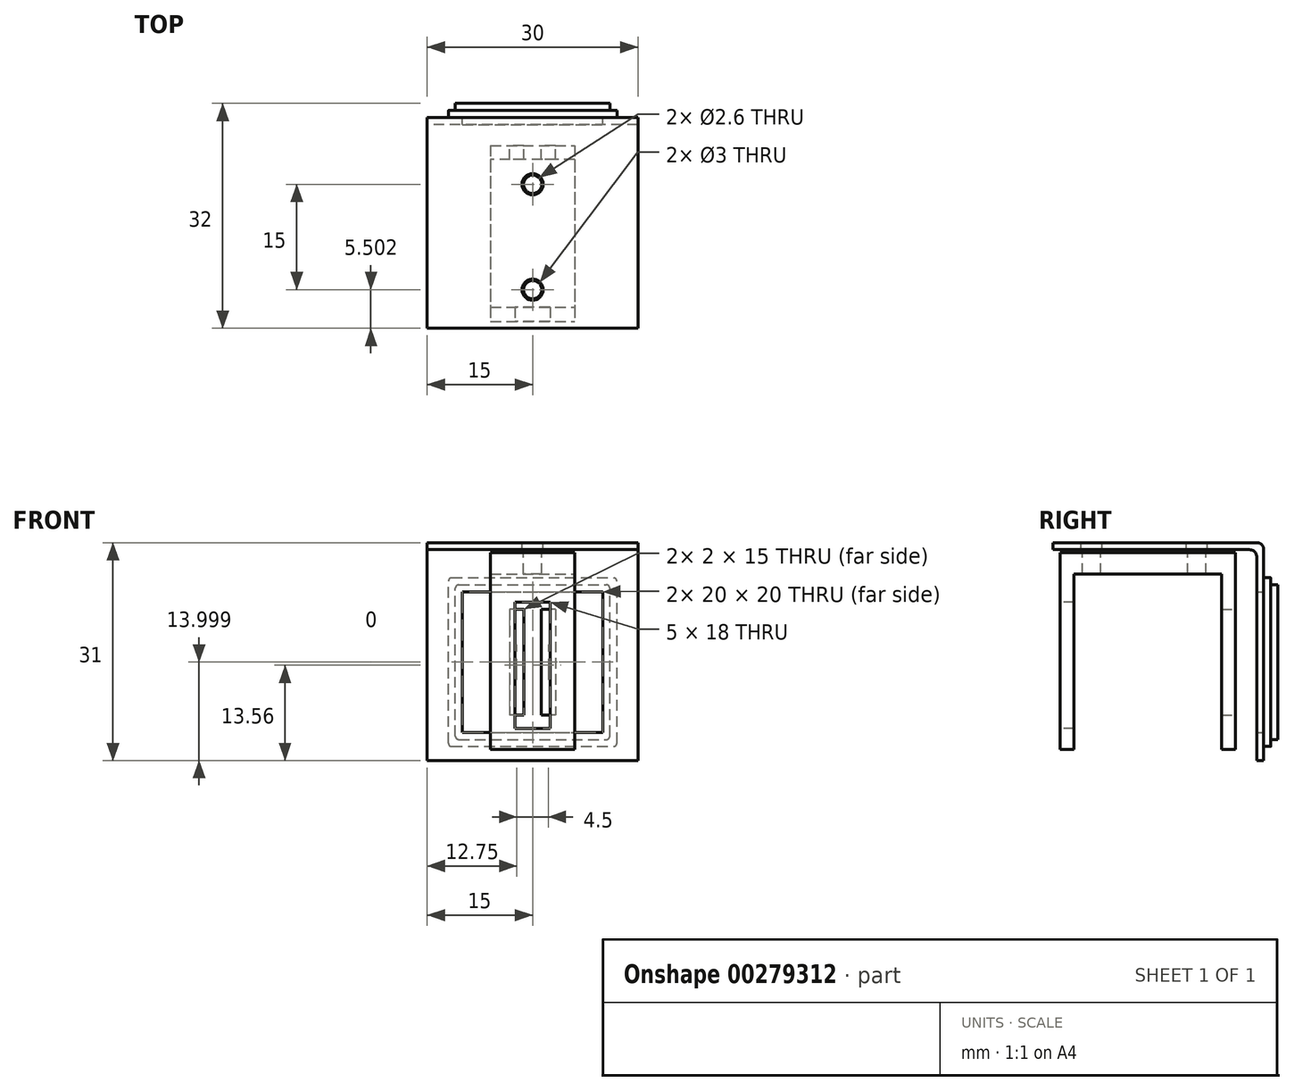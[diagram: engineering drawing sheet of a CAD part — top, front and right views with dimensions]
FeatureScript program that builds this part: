
annotation { "Feature Type Name" : "Feature", "Feature Type Description" : "" }
export const myFeature = defineFeature(function(context is Context, id is Id, definition is map)
    precondition{}
    {
        {
            var Q0;
            Q0=qCreatedBy(makeId("Right.planeOp"),FACE);
            var sketch = newSketch(context, id + "F0", { "sketchPlane" : qUnion([Q0])});
            skLineSegment(sketch, "E0.bottom", {"start": v(-2.16, 1.44) * mm, "end": v(27.84, 1.44) * mm});
            skLineSegment(sketch, "E0.top", {"start": v(-2.16, 0.44) * mm, "end": v(27.84, 0.44) * mm});
            skLineSegment(sketch, "E0.left", {"start": v(-2.16, 1.44) * mm, "end": v(-2.16, 0.44) * mm});
            skLineSegment(sketch, "E0.right", {"start": v(27.84, 1.44) * mm, "end": v(27.84, 0.44) * mm});
            skLineSegment(sketch, "E1.bottom", {"start": v(27.84, 0.44) * mm, "end": v(26.84, 0.44) * mm});
            skLineSegment(sketch, "E1.top", {"start": v(27.84, -29.56) * mm, "end": v(26.84, -29.56) * mm});
            skLineSegment(sketch, "E1.left", {"start": v(27.84, 0.44) * mm, "end": v(27.84, -29.56) * mm});
            skLineSegment(sketch, "E1.right", {"start": v(26.84, 0.44) * mm, "end": v(26.84, -29.56) * mm});
            skSolve(sketch);
        }
        {
            var Q0;
            Q0 = qSketchRegion(id + "F0", true);
            extrude(context, id + "F1", {"entities" : qUnion([Q0]), "depth" : 30 * mm});
        }
        {
            var Q0;
            Q0=makeQuery(id+"F1.opExtrude","SWEPT_EDGE",EDGE,{"disambiguationData":[OSD([sQuery(id+"F0.wireOp",EDGE,"E0.bottom"),sQuery(id+"F0.wireOp",EDGE,"E0.right")])]});
            var Q1;
            Q1=makeQuery(id+"F1.opExtrude","SWEPT_EDGE",EDGE,{"disambiguationData":[OSD([sQuery(id+"F0.wireOp",EDGE,"E0.top"),sQuery(id+"F0.wireOp",EDGE,"E1.bottom"),sQuery(id+"F0.wireOp",EDGE,"E1.right")])]});
            fillet(context, id + "F2", {"entities" : qUnion([Q0, Q1]), "radius" : 1 * mm, "tangentPropagation" : true, "allowEdgeOverflow" : false});
        }
        {
            var Q0;
            Q0=makeQuery(id+"F1.opExtrude","SWEPT_FACE",FACE,{"disambiguationData":[OSD([sQuery(id+"F0.wireOp",EDGE,"E0.right"),sQuery(id+"F0.wireOp",EDGE,"E1.left")])]});
            var sketch = newSketch(context, id + "F3", { "sketchPlane" : qUnion([Q0])});
            skLineSegment(sketch, "E2.bottom", {"start": v(-5, -25.56) * mm, "end": v(-25, -25.56) * mm});
            skLineSegment(sketch, "E2.top", {"start": v(-5, -5.56) * mm, "end": v(-25, -5.56) * mm});
            skLineSegment(sketch, "E2.left", {"start": v(-5, -25.56) * mm, "end": v(-5, -5.56) * mm});
            skLineSegment(sketch, "E2.right", {"start": v(-25, -25.56) * mm, "end": v(-25, -5.56) * mm});
            skPoint(sketch, "E2.middle", {"position": v(-15, -15.56) * mm});
            skPoint(sketch, "E3", {"position": v(-15, -29.56) * mm});
            skSolve(sketch);
        }
        {
            var Q0;
            Q0 = qSketchRegion(id + "F3", true);
            extrude(context, id + "F4", {"entities" : qUnion([Q0]), "operationType" : NewBodyOperationType.REMOVE, "oppositeDirection" : true, "depth" : 1 * mm});
        }
        {
            var Q0;
            Q0=makeQuery(id+"F1.opExtrude","SWEPT_FACE",FACE,{"disambiguationData":[OSD([sQuery(id+"F0.wireOp",EDGE,"E0.bottom")])]});
            var sketch = newSketch(context, id + "F5", { "sketchPlane" : qUnion([Q0])});
            skCircle(sketch, "E4", {"center": v(15, 18.34) * mm, "radius": 1.5 * mm});
            skPoint(sketch, "E4.centerSnap0", {"position": v(15, 26.84) * mm});
            skCircle(sketch, "E5", {"center": v(15, 3.34) * mm, "radius": 1.5 * mm});
            skSolve(sketch);
        }
        {
            var Q0;
            Q0=sQuery(id+"F5.wireOp",VERTEX,"E5.center");
            var Q1;
            Q1=sQuery(id+"F5.wireOp",VERTEX,"E4.center");
            var Q2;
            Q2=makeQuery(id+"F1.opExtrude","SWEPT_BODY",BODY,{"disambiguationData":[OSD([sQuery(id+"F0.wireOp",EDGE,"E0.bottom"),sQuery(id+"F0.wireOp",EDGE,"E0.top"),sQuery(id+"F0.wireOp",EDGE,"E0.left"),sQuery(id+"F0.wireOp",EDGE,"E0.right"),sQuery(id+"F0.wireOp",EDGE,"E1.top"),sQuery(id+"F0.wireOp",EDGE,"E1.left"),sQuery(id+"F0.wireOp",EDGE,"E1.right")])]});
            hole(context, id + "F6", {"style" : HoleStyle.SIMPLE, "endStyle" : HoleEndStyle.BLIND, "holeDiameter" : 3 * mm, "holeDepth" : 1 * mm, "tappedDepth" : 12 * mm, "tapClearance" : 3, "locations" : qUnion([Q0, Q1]), "scope" : qUnion([Q2])});
        }
        {
            var Q0;
            Q0=qCreatedBy(makeId("Top.planeOp"),FACE);
            var sketch = newSketch(context, id + "F7", { "sketchPlane" : qUnion([Q0])});
            skLineSegment(sketch, "E6.bottom", {"start": v(9, 23.84) * mm, "end": v(21, 23.84) * mm});
            skLineSegment(sketch, "E6.top", {"start": v(9, -1.16) * mm, "end": v(21, -1.16) * mm});
            skLineSegment(sketch, "E6.left", {"start": v(9, 23.84) * mm, "end": v(9, -1.16) * mm});
            skLineSegment(sketch, "E6.right", {"start": v(21, 23.84) * mm, "end": v(21, -1.16) * mm});
            skPoint(sketch, "E6.middle", {"position": v(15, 11.34) * mm});
            skCircle(sketch, "E7", {"center": v(15, 18.34) * mm, "radius": 1.3 * mm});
            skCircle(sketch, "E8", {"center": v(15, 3.34) * mm, "radius": 1.3 * mm});
            skSolve(sketch);
        }
        {
            var Q0;
            Q0 = qSketchRegion(id + "F7", true);
            extrude(context, id + "F8", {"entities" : qUnion([Q0]), "oppositeDirection" : true, "depth" : 3 * mm});
        }
        {
            var Q0;
            Q0=makeQuery(id+"F8.opExtrude","CAP_FACE",FACE,{"disambiguationData":[OSD([sQuery(id+"F7.wireOp",EDGE,"E6.bottom"),sQuery(id+"F7.wireOp",EDGE,"E6.top"),sQuery(id+"F7.wireOp",EDGE,"E6.left"),sQuery(id+"F7.wireOp",EDGE,"E6.right")])],"isStart":false});
            var sketch = newSketch(context, id + "F9", { "sketchPlane" : qUnion([Q0])});
            skLineSegment(sketch, "E9.bottom", {"start": v(21, -23.84) * mm, "end": v(9, -23.84) * mm});
            skLineSegment(sketch, "E9.top", {"start": v(21, -21.84) * mm, "end": v(9, -21.84) * mm});
            skLineSegment(sketch, "E9.left", {"start": v(21, -23.84) * mm, "end": v(21, -21.84) * mm});
            skLineSegment(sketch, "E9.right", {"start": v(9, -23.84) * mm, "end": v(9, -21.84) * mm});
            skLineSegment(sketch, "E10.bottom", {"start": v(9, 1.16) * mm, "end": v(21, 1.16) * mm});
            skLineSegment(sketch, "E10.top", {"start": v(9, -0.84) * mm, "end": v(21, -0.84) * mm});
            skLineSegment(sketch, "E10.left", {"start": v(9, 1.16) * mm, "end": v(9, -0.84) * mm});
            skLineSegment(sketch, "E10.right", {"start": v(21, 1.16) * mm, "end": v(21, -0.84) * mm});
            skSolve(sketch);
        }
        {
            var Q0;
            Q0 = qSketchRegion(id + "F9", true);
            extrude(context, id + "F10", {"entities" : qUnion([Q0]), "operationType" : NewBodyOperationType.ADD, "depth" : 25 * mm});
        }
        {
            var Q0;
            Q0=makeQuery(id+"F10.boolean.opBoolean","MERGE",FACE,{"derivedFrom":[makeQuery(id+"F8.opExtrude","SWEPT_FACE",FACE,{"disambiguationData":[OSD([sQuery(id+"F7.wireOp",EDGE,"E6.bottom")])]}),makeQuery(id+"F10.opExtrude","SWEPT_FACE",FACE,{"disambiguationData":[OSD([sQuery(id+"F9.wireOp",EDGE,"E9.bottom")])]})]});
            var sketch = newSketch(context, id + "F11", { "sketchPlane" : qUnion([Q0])});
            skLineSegment(sketch, "E11.bottom", {"start": v(-18.25, -8.06) * mm, "end": v(-16.25, -8.06) * mm});
            skLineSegment(sketch, "E11.top", {"start": v(-18.25, -23.06) * mm, "end": v(-16.25, -23.06) * mm});
            skLineSegment(sketch, "E11.left", {"start": v(-18.25, -8.06) * mm, "end": v(-18.25, -23.06) * mm});
            skLineSegment(sketch, "E11.right", {"start": v(-16.25, -8.06) * mm, "end": v(-16.25, -23.06) * mm});
            skLineSegment(sketch, "E12.bottom", {"start": v(-13.75, -8.06) * mm, "end": v(-11.75, -8.06) * mm});
            skLineSegment(sketch, "E12.top", {"start": v(-13.75, -23.06) * mm, "end": v(-11.75, -23.06) * mm});
            skLineSegment(sketch, "E12.left", {"start": v(-13.75, -8.06) * mm, "end": v(-13.75, -23.06) * mm});
            skLineSegment(sketch, "E12.right", {"start": v(-11.75, -8.06) * mm, "end": v(-11.75, -23.06) * mm});
            skSolve(sketch);
        }
        {
            var Q0;
            Q0 = qSketchRegion(id + "F11", true);
            extrude(context, id + "F12", {"entities" : qUnion([Q0]), "operationType" : NewBodyOperationType.REMOVE, "oppositeDirection" : true, "depth" : 3 * mm});
        }
        {
            var Q0;
            Q0=makeQuery(id+"F10.boolean.opBoolean","MERGE",FACE,{"derivedFrom":[makeQuery(id+"F8.opExtrude","SWEPT_FACE",FACE,{"disambiguationData":[OSD([sQuery(id+"F7.wireOp",EDGE,"E6.top")])]}),makeQuery(id+"F10.opExtrude","SWEPT_FACE",FACE,{"disambiguationData":[OSD([sQuery(id+"F9.wireOp",EDGE,"E10.bottom")])]})]});
            var sketch = newSketch(context, id + "F13", { "sketchPlane" : qUnion([Q0])});
            skLineSegment(sketch, "E13.bottom", {"start": v(17.5, -25) * mm, "end": v(12.5, -25) * mm});
            skLineSegment(sketch, "E13.top", {"start": v(17.5, -7) * mm, "end": v(12.5, -7) * mm});
            skLineSegment(sketch, "E13.left", {"start": v(17.5, -25) * mm, "end": v(17.5, -7) * mm});
            skLineSegment(sketch, "E13.right", {"start": v(12.5, -25) * mm, "end": v(12.5, -7) * mm});
            skPoint(sketch, "E13.middle", {"position": v(15, -16) * mm});
            skPoint(sketch, "E13.middle.positionSnap0", {"position": v(15, 0) * mm});
            skPoint(sketch, "E13.centerSnap0", {"position": v(15, 0) * mm});
            skSolve(sketch);
        }
        {
            var Q0;
            Q0 = qSketchRegion(id + "F13", true);
            extrude(context, id + "F14", {"entities" : qUnion([Q0]), "operationType" : NewBodyOperationType.REMOVE, "oppositeDirection" : true, "depth" : 2 * mm});
        }
        {
            var Q0;
            Q0=makeQuery(id+"F1.opExtrude","SWEPT_FACE",FACE,{"disambiguationData":[OSD([sQuery(id+"F0.wireOp",EDGE,"E0.right"),sQuery(id+"F0.wireOp",EDGE,"E1.left")])]});
            var sketch = newSketch(context, id + "F15", { "sketchPlane" : qUnion([Q0])});
            skLineSegment(sketch, "E14.bottom", {"start": v(-5, -25.56) * mm, "end": v(-25, -25.56) * mm});
            skLineSegment(sketch, "E14.top", {"start": v(-5, -5.56) * mm, "end": v(-25, -5.56) * mm});
            skLineSegment(sketch, "E14.left", {"start": v(-5, -25.56) * mm, "end": v(-5, -5.56) * mm});
            skLineSegment(sketch, "E14.right", {"start": v(-25, -25.56) * mm, "end": v(-25, -5.56) * mm});
            skPoint(sketch, "E14.middle", {"position": v(-15, -15.56) * mm});
            skPoint(sketch, "E14.middle.positionSnap0", {"position": v(-25, -15.56) * mm});
            skPoint(sketch, "E14.middle.positionSnap1", {"position": v(-15, -5.56) * mm});
            skPoint(sketch, "E14.centerSnap0", {"position": v(-25, -15.56) * mm});
            skPoint(sketch, "E14.centerSnap1", {"position": v(-15, -5.56) * mm});
            skLineSegment(sketch, "E15.bottom", {"start": v(-3, -27.56) * mm, "end": v(-27, -27.56) * mm});
            skLineSegment(sketch, "E15.top", {"start": v(-3, -3.56) * mm, "end": v(-27, -3.56) * mm});
            skLineSegment(sketch, "E15.left", {"start": v(-3, -27.56) * mm, "end": v(-3, -3.56) * mm});
            skLineSegment(sketch, "E15.right", {"start": v(-27, -27.56) * mm, "end": v(-27, -3.56) * mm});
            skSolve(sketch);
        }
        {
            var Q0;
            Q0 = qSketchRegion(id + "F15", true);
            extrude(context, id + "F16", {"entities" : qUnion([Q0]), "depth" : 2 * mm});
        }
        {
            var Q0;
            Q0=makeQuery(id+"F16.opExtrude","CAP_FACE",FACE,{"disambiguationData":[OSD([sQuery(id+"F15.wireOp",EDGE,"E14.bottom"),sQuery(id+"F15.wireOp",EDGE,"E14.top"),sQuery(id+"F15.wireOp",EDGE,"E14.left"),sQuery(id+"F15.wireOp",EDGE,"E14.right"),sQuery(id+"F15.wireOp",EDGE,"E15.bottom"),sQuery(id+"F15.wireOp",EDGE,"E15.top"),sQuery(id+"F15.wireOp",EDGE,"E15.left"),sQuery(id+"F15.wireOp",EDGE,"E15.right")])],"isStart":false});
            var sketch = newSketch(context, id + "F17", { "sketchPlane" : qUnion([Q0])});
            skLineSegment(sketch, "E16.bottom", {"start": v(-3, -27.56) * mm, "end": v(-27, -27.56) * mm});
            skLineSegment(sketch, "E16.top", {"start": v(-3, -3.56) * mm, "end": v(-27, -3.56) * mm});
            skLineSegment(sketch, "E16.left", {"start": v(-3, -27.56) * mm, "end": v(-3, -3.56) * mm});
            skLineSegment(sketch, "E16.right", {"start": v(-27, -27.56) * mm, "end": v(-27, -3.56) * mm});
            skPoint(sketch, "E16.middle", {"position": v(-15, -15.56) * mm});
            skPoint(sketch, "E16.middle.positionSnap0", {"position": v(-25, -15.56) * mm});
            skPoint(sketch, "E16.middle.positionSnap1", {"position": v(-15, -5.56) * mm});
            skPoint(sketch, "E16.centerSnap0", {"position": v(-25, -15.56) * mm});
            skPoint(sketch, "E16.centerSnap1", {"position": v(-15, -5.56) * mm});
            skLineSegment(sketch, "E17.bottom", {"start": v(-4, -26.56) * mm, "end": v(-26, -26.56) * mm});
            skLineSegment(sketch, "E17.top", {"start": v(-4, -4.56) * mm, "end": v(-26, -4.56) * mm});
            skLineSegment(sketch, "E17.left", {"start": v(-4, -26.56) * mm, "end": v(-4, -4.56) * mm});
            skLineSegment(sketch, "E17.right", {"start": v(-26, -26.56) * mm, "end": v(-26, -4.56) * mm});
            skSolve(sketch);
        }
        {
            var Q0;
            Q0 = qSketchRegion(id + "F17", true);
            extrude(context, id + "F18", {"entities" : qUnion([Q0]), "operationType" : NewBodyOperationType.REMOVE, "oppositeDirection" : true, "depth" : 1 * mm});
        }
        {
            var Q0;
            Q0=makeQuery(id+"F18.boolean.opBoolean","COPY",EDGE,{"derivedFrom":makeQuery(id+"F18.opExtrude","SWEPT_EDGE",EDGE,{"disambiguationData":[OSD([sQuery(id+"F17.wireOp",EDGE,"E17.top"),sQuery(id+"F17.wireOp",EDGE,"E17.right")])]})});
            var Q1;
            Q1=makeQuery(id+"F18.boolean.opBoolean","COPY",EDGE,{"derivedFrom":makeQuery(id+"F18.opExtrude","SWEPT_EDGE",EDGE,{"disambiguationData":[OSD([sQuery(id+"F17.wireOp",EDGE,"E17.top"),sQuery(id+"F17.wireOp",EDGE,"E17.left")])]})});
            var Q2;
            Q2=makeQuery(id+"F18.boolean.opBoolean","COPY",EDGE,{"derivedFrom":makeQuery(id+"F18.opExtrude","SWEPT_EDGE",EDGE,{"disambiguationData":[OSD([sQuery(id+"F17.wireOp",EDGE,"E17.bottom"),sQuery(id+"F17.wireOp",EDGE,"E17.left")])]})});
            var Q3;
            Q3=makeQuery(id+"F18.boolean.opBoolean","COPY",EDGE,{"derivedFrom":makeQuery(id+"F18.opExtrude","SWEPT_EDGE",EDGE,{"disambiguationData":[OSD([sQuery(id+"F17.wireOp",EDGE,"E17.bottom"),sQuery(id+"F17.wireOp",EDGE,"E17.right")])]})});
            var Q4;
            Q4=makeQuery(id+"F16.opExtrude","SWEPT_EDGE",EDGE,{"disambiguationData":[OSD([sQuery(id+"F15.wireOp",EDGE,"E15.top"),sQuery(id+"F15.wireOp",EDGE,"E15.right")])]});
            var Q5;
            Q5=makeQuery(id+"F16.opExtrude","SWEPT_EDGE",EDGE,{"disambiguationData":[OSD([sQuery(id+"F15.wireOp",EDGE,"E15.top"),sQuery(id+"F15.wireOp",EDGE,"E15.left")])]});
            var Q6;
            Q6=makeQuery(id+"F16.opExtrude","SWEPT_EDGE",EDGE,{"disambiguationData":[OSD([sQuery(id+"F15.wireOp",EDGE,"E15.bottom"),sQuery(id+"F15.wireOp",EDGE,"E15.right")])]});
            var Q7;
            Q7=makeQuery(id+"F16.opExtrude","SWEPT_EDGE",EDGE,{"disambiguationData":[OSD([sQuery(id+"F15.wireOp",EDGE,"E15.bottom"),sQuery(id+"F15.wireOp",EDGE,"E15.left")])]});
            fillet(context, id + "F19", {"entities" : qUnion([Q0, Q1, Q2, Q3, Q4, Q5, Q6, Q7]), "radius" : 0.5 * mm, "tangentPropagation" : true, "allowEdgeOverflow" : false});
        }
    });
